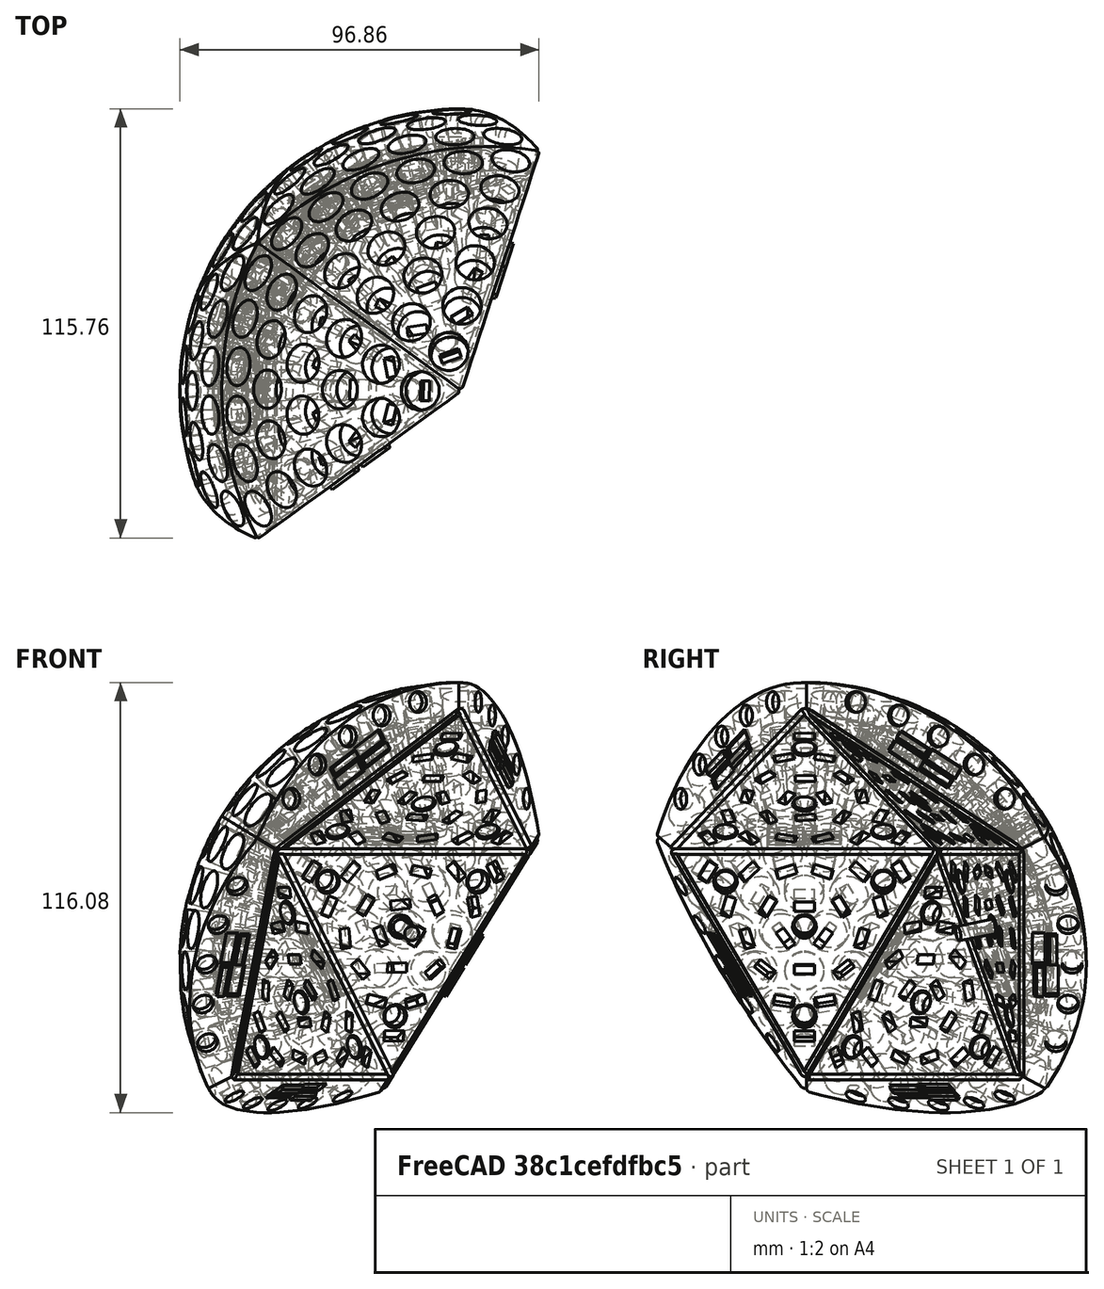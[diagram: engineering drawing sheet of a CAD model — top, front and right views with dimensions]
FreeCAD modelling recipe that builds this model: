
FCSTD DOCUMENT  (FreeCAD 0.20R27422 (Git))
Label: assembly_a4
License: All rights reserved
LicenseURL: http://en.wikipedia.org/wiki/All_rights_reserved
objects: Part::Part2DObjectPython×7, App::Link×5, App::DocumentObjectGroup×3, PartDesign::CoordinateSystem×1, App::FeaturePython×1, App::Part×1, Part::FeaturePython×1, Part::Cylinder×1, Part::Compound×1, PartDesign::Body×1
note: 12 computed .brp shape members not serialized (recipe doc carries the construction recipe); baked Part::Feature solids carry a one-line shape summary decoded from their .brp
EXTERNAL_REF file=Shell_rev1.FCStd obj=Body
EXTERNAL_REF file=Shell_rev1.FCStd obj=Local_CS001
EXTERNAL_REF file=Shell_rev1.FCStd obj=Local_CS002

FEATURE [App::DocumentObjectGroup] Parts
FEATURE [PartDesign::CoordinateSystem] LCS_Origin
  AttacherType = Attacher::AttachEngine3D
  MapMode = 2
  Support = -> [X_Axis]
FEATURE [App::FeaturePython] Variables  # WARN: FeaturePython — macro-defined, semantics opaque (R4)
  Type = App::PropertyContainer
FEATURE [App::DocumentObjectGroup] Constraints
FEATURE [App::DocumentObjectGroup] Configurations
FEATURE [App::Link] ShellBody
  LinkPlacement = pos=(-18,2.14577e-06,0) rot=(0,0,1;0rad)
  LinkedObject = -> <external Shell_rev1.FCStd>#Body
  Placement = pos=(-18,2.14577e-06,0) rot=(0,0,1;0rad)
FEATURE [App::Link] ShellBody2
  AttachedBy = #Local_CS001
  AttachedTo = ShellBody#Local_CS001
  AttachmentOffset = pos=(0,0,0) rot=(0,1,0;3.14159rad)
  LinkPlacement = pos=(-18,2.14577e-06,8.54e-14) rot=(0.951057,-0.309017,0;3.14159rad)
  LinkedObject = -> <external Shell_rev1.FCStd>#Body
  Placement = pos=(-18,2.14577e-06,8.54e-14) rot=(0.951057,-0.309017,0;3.14159rad)
  SolverId = Asm4EE
  expr: Placement = ShellBody.Placement * Shell_rev1#Local_CS001.Placement * AttachmentOffset * Shell_rev1#Local_CS001.Placement ^ -1
FEATURE [App::Link] ShellBody3
  AssemblyType = Part::Link
  AttachedBy = #Local_CS001
  AttachedTo = ShellBody2#Local_CS002
  AttachmentOffset = pos=(0,0,0) rot=(0,-1,0;3.14159rad)
  LinkPlacement = pos=(-18,2.14577e-06,1.78e-13) rot=(-0.794654,0.57735,-0.187592;2.0944rad)
  LinkedObject = -> <external Shell_rev1.FCStd>#Body
  Placement = pos=(-18,2.14577e-06,1.78e-13) rot=(-0.794654,0.57735,-0.187592;2.0944rad)
  SolverId = Asm4EE
  expr: Placement = ShellBody2.Placement * Shell_rev1#Local_CS002.Placement * AttachmentOffset * Shell_rev1#Local_CS001.Placement ^ -1
FEATURE [App::Link] ShellBody4
  AssemblyType = Part::Link
  AttachedBy = #Local_CS001
  AttachedTo = ShellBody3#Local_CS002
  AttachmentOffset = pos=(0,0,0) rot=(0,-1,0;3.14159rad)
  LinkPlacement = pos=(-18,2.14577e-06,1.705e-13) rot=(0.276393,-0.850651,0.447214;5.02655rad)
  LinkedObject = -> <external Shell_rev1.FCStd>#Body
  Placement = pos=(-18,2.14577e-06,1.705e-13) rot=(0.276393,-0.850651,0.447214;5.02655rad)
  SolverId = Asm4EE
  expr: Placement = ShellBody3.Placement * Shell_rev1#Local_CS002.Placement * AttachmentOffset * Shell_rev1#Local_CS001.Placement ^ -1
FEATURE [App::Link] ShellBody5
  AssemblyType = Part::Link
  AttachedBy = #Local_CS001
  AttachedTo = ShellBody4#Local_CS002
  AttachmentOffset = pos=(0,0,0) rot=(0,-1,0;3.14159rad)
  LinkPlacement = pos=(-18,2.14577e-06,9.95e-14) rot=(0.723607,0.525731,-0.447214;1.25664rad)
  LinkedObject = -> <external Shell_rev1.FCStd>#Body
  Placement = pos=(-18,2.14577e-06,9.95e-14) rot=(0.723607,0.525731,-0.447214;1.25664rad)
  SolverId = Asm4EE
  expr: Placement = ShellBody4.Placement * Shell_rev1#Local_CS002.Placement * AttachmentOffset * Shell_rev1#Local_CS001.Placement ^ -1
FEATURE [App::Part] Assembly
  AssemblyType = Part::Link
  Group = -> [LCS_Origin,Variables,Constraints,Configurations,ShellBody2,ShellBody,ShellBody3,ShellBody4,ShellBody5]
  Origin = -> Origin
  Type = Assembly
FEATURE [Part::Part2DObjectPython] Wire  # Draft 2D object (typed FeaturePython)
  Area = 0
  ChamferSize = 0
  Closed = true
  End = (-28.2005,31.4412,43.2827)
  FilletRadius = 0
  Length = 194.384
  MakeFace = false
  Placement = pos=(-34.5172,50.8819,10.2082) rot=(0,1,0;1.00987rad)
  Points = (5) [(0,0,0),(3.07448,-19.4407,-33.5317),(-19.6899,-50.8819,-31.2948),(-36.8036,-50.8965,3.59149),(-24.646,-19.4407,22.9434)]
  Start = (-34.5172,50.8819,10.2082)
  Subdivisions = 0
FEATURE [Part::Part2DObjectPython] Line001  # Draft 2D object (typed FeaturePython)
  Area = 0
  ChamferSize = 0
  Closed = false
  End = (-34.5306,50.8759,10.2165)
  FilletRadius = 0
  Length = 5
  MakeFace = false
  Placement = pos=(-36.0482,55.5467,11.1544) rot=(-0.699935,-0.648304,0.299653;1.16725rad)
  Points = (2) [(0,0,0),(-1.96669,-2.31198,-3.97327)]
  Start = (-36.0482,55.5467,11.1544)
  Subdivisions = 0
FEATURE [Part::Part2DObjectPython] Line004  # Draft 2D object (typed FeaturePython)
  Area = 0
  ChamferSize = 0
  Closed = false
  End = (-47.8961,41.1615,-0.0124104)
  FilletRadius = 0
  Length = 59.8324
  MakeFace = false
  Placement = pos=(-51.0545,-0.0145872,43.2827) rot=(-0.699935,-0.648304,0.299653;1.16725rad)
  Points = (2) [(0,0,0),(4.57589,59.6572,-1.56319e-13)]
  Start = (-51.0545,-0.0145872,43.2827)
  Subdivisions = 0
FEATURE [Part::FeaturePython] Point  # WARN: FeaturePython — macro-defined, semantics opaque (R4)
  Placement = pos=(-49.3086,22.747,19.3498) rot=(0,0,1;0rad)
  X = -49.3086
  Y = 22.747
  Z = 19.3498
FEATURE [Part::Cylinder] Cylinder
  Angle = 360
  AttacherType = Attacher::AttachEngine3D
  FirstAngle = 0
  Height = 10
  Placement = pos=(-31.4819,41.5402,8.33226) rot=(-0.393336,-0.672763,-0.626639;1.91525rad)
  Radius = 2
  SecondAngle = 0
FEATURE [Part::Compound] Compound
  Links = -> [ShellBody2,ShellBody,ShellBody3,ShellBody4,ShellBody5]
FEATURE [Part::Part2DObjectPython] Line007  # Draft 2D object (typed FeaturePython)
  Area = 0
  ChamferSize = 0
  Closed = false
  End = (-5.89216,-8.79686,-7.48306)
  FilletRadius = 0
  Length = 60
  MakeFace = false
  Placement = pos=(-49.3086,22.747,19.3498) rot=(-0.699935,-0.648304,0.299653;1.16725rad)
  Points = (2) [(0,0,0),(1.47438e-13,-1.24345e-14,-60)]
  Start = (-49.3086,22.747,19.3498)
  Subdivisions = 0
FEATURE [Part::Part2DObjectPython] Line008  # Draft 2D object (typed FeaturePython)
  Area = 0
  ChamferSize = 0
  Closed = false
  End = (-34.5172,50.8819,10.2082)
  FilletRadius = 0
  Length = 33.0745
  MakeFace = false
  Placement = pos=(-49.3086,22.747,19.3498) rot=(-0.699935,-0.648304,0.299653;1.16725rad)
  Points = (2) [(0,0,0),(21.4302,25.1927,-1.13687e-13)]
  Start = (-49.3086,22.747,19.3498)
  Subdivisions = 0
FEATURE [Part::Part2DObjectPython] Line009  # Draft 2D object (typed FeaturePython)
  Area = 0
  ChamferSize = 0
  Closed = false
  End = (-43.5584,18.5693,15.796)
  FilletRadius = 0
  Length = 27.0039
  MakeFace = false
  Placement = pos=(-31.4819,41.5402,8.33226) rot=(0,1,0;0.553574rad)
  Points = (2) [(0,0,0),(-14.1968,-22.9709,-2.30926e-14)]
  Start = (-31.4819,41.5402,8.33226)
  Subdivisions = 0
FEATURE [Part::Part2DObjectPython] Line  # Draft 2D object (typed FeaturePython)
  Area = 0
  ChamferSize = 0
  Closed = false
  End = (-33.0438,18.5693,32.809)
  FilletRadius = 0
  Length = 20
  MakeFace = false
  Placement = pos=(-43.5584,18.5693,15.796) rot=(0,1,0;0.553574rad)
  Points = (2) [(0,0,0),(0,3.55271e-15,20)]
  Start = (-43.5584,18.5693,15.796)
  Subdivisions = 0
FEATURE [PartDesign::Body] Body
  Origin = -> Origin001

RESOLVED EXTERNAL PARTS (link-assembly join: the EXTERNAL_REF files above that resolve inside this repo's crawl, each included once):
---- part Shell_rev1.FCStd = doc fcstd_350f59060ad1 ----
FCSTD DOCUMENT  (FreeCAD 0.20R27422 (Git))
Label: Shell_rev1
License: All rights reserved
LicenseURL: http://en.wikipedia.org/wiki/All_rights_reserved
objects: PartDesign::CoordinateSystem×9, Part::Feature×3, Part::Chamfer×3, Part::Part2DObjectPython×1, Part::Fillet×1, PartDesign::FeatureBase×1, PartDesign::Body×1
note: 19 computed .brp shape members not serialized (recipe doc carries the construction recipe); baked Part::Feature solids carry a one-line shape summary decoded from their .brp

FEATURE [Part::Part2DObjectPython] Line  # Draft 2D object (typed FeaturePython)
  Area = 0
  ChamferSize = 0
  Closed = false
  End = (-60.4609,0,-2.48e-14)
  FilletRadius = 0
  Length = 60.4609
  MakeFace = true
  Points = (2) [(0,0,0),(-60.4609,0,-2.4803e-14)]
  Start = (0,0,0)
  Subdivisions = 0
FEATURE [Part::Feature] Shape
  Placement = pos=(0,0,0) rot=(0,1,0;0.188711rad)
  shape: bbox 26.49 x 83.96 x 75.99 mm, 229 faces (baked)
FEATURE [Part::Feature] Shape001
  Placement = pos=(0,0,0) rot=(0,1,0;0.188711rad)
  shape: bbox 11.8 x 62.95 x 53.85 mm, 54 faces (baked)
FEATURE [Part::Feature] Shape002
  shape: bbox 23.55 x 50.22 x 45.22 mm, 59 faces (baked)
FEATURE [Part::Fillet] Fillet
  Base = -> Shape
  Edges = 3 edges r=1: [Edge25,Edge27,Edge50]
FEATURE [Part::Chamfer] Chamfer
  Base = -> Fillet
  Edges = 1 edges r=1: [Edge79]
FEATURE [Part::Chamfer] Chamfer001
  Base = -> Chamfer
  Edges = 4 edges r=0.4: [Edge150,Edge171,Edge184,Edge225]
FEATURE [Part::Chamfer] Chamfer002  label="shell"
  Base = -> Chamfer001
  Edges = 6 edges r=0.8: [Edge443,Edge453,Edge487,Edge499,Edge530,Edge542]
FEATURE [PartDesign::FeatureBase] BaseFeature
  BaseFeature = -> Chamfer002
FEATURE [PartDesign::CoordinateSystem] Local_CS
  AttacherType = Attacher::AttachEngine3D
  MapMode = 11
  Placement = pos=(-61.4889,-9e-15,38.0022) rot=(0.693258,0.693258,-0.19694;3.5305rad)
  Support = -> [BaseFeature]
FEATURE [PartDesign::CoordinateSystem] Local_CS001
  AttacherType = Attacher::AttachEngine3D
  MapMode = 11
  Placement = pos=(-68.7467,22.3371,-2.28e-14) rot=(0.459079,0.33354,-0.823406;2.06334rad)
  Support = -> [BaseFeature]
FEATURE [PartDesign::CoordinateSystem] Local_CS002
  AttacherType = Attacher::AttachEngine3D
  MapMode = 11
  Placement = pos=(-68.7467,-22.3371,-2.13e-14) rot=(-0.404509,-0.556759,-0.725529;1.57219rad)
  Support = -> [BaseFeature]
FEATURE [PartDesign::CoordinateSystem] Local_CS003
  AttacherType = Attacher::AttachEngine3D
  MapMode = 11
  Placement = pos=(-57.7484,-24.8267,35.6905) rot=(0.693258,0.693258,-0.19694;3.5305rad)
  Support = -> [BaseFeature]
FEATURE [PartDesign::CoordinateSystem] Local_CS004
  AttacherType = Attacher::AttachEngine3D
  MapMode = 11
  Placement = pos=(-68.598,-8.56496,-21.1189) rot=(-0.404509,-0.556759,-0.725529;1.57219rad)
  Support = -> [BaseFeature]
FEATURE [PartDesign::CoordinateSystem] Local_CS005
  AttacherType = Attacher::AttachEngine3D
  MapMode = 11
  Placement = pos=(-60.5313,33.3917,21.1189) rot=(0.459079,0.33354,-0.823406;2.06334rad)
  Support = -> [BaseFeature]
FEATURE [PartDesign::CoordinateSystem] Local_CS006
  AttacherType = Attacher::AttachEngine3D
  MapMode = 11
  Placement = pos=(-57.7484,24.8267,35.6905) rot=(0.693258,0.693258,-0.19694;3.5305rad)
  Support = -> [BaseFeature]
FEATURE [PartDesign::CoordinateSystem] Local_CS007
  AttacherType = Attacher::AttachEngine3D
  MapMode = 11
  Placement = pos=(-60.5313,-33.3917,21.1189) rot=(-0.404509,-0.556759,-0.725529;1.57219rad)
  Support = -> [BaseFeature]
FEATURE [PartDesign::CoordinateSystem] Local_CS008
  AttacherType = Attacher::AttachEngine3D
  MapMode = 11
  Placement = pos=(-68.598,8.56496,-21.1189) rot=(0.459079,0.33354,-0.823406;2.06334rad)
  Support = -> [BaseFeature]
FEATURE [PartDesign::Body] Body
  BaseFeature = -> Chamfer002
  Group = -> [BaseFeature,Local_CS,Local_CS001,Local_CS002,Local_CS003,Local_CS004,Local_CS005,Local_CS006,Local_CS007,Local_CS008]
  Origin = -> Origin
  Tip = -> BaseFeature
